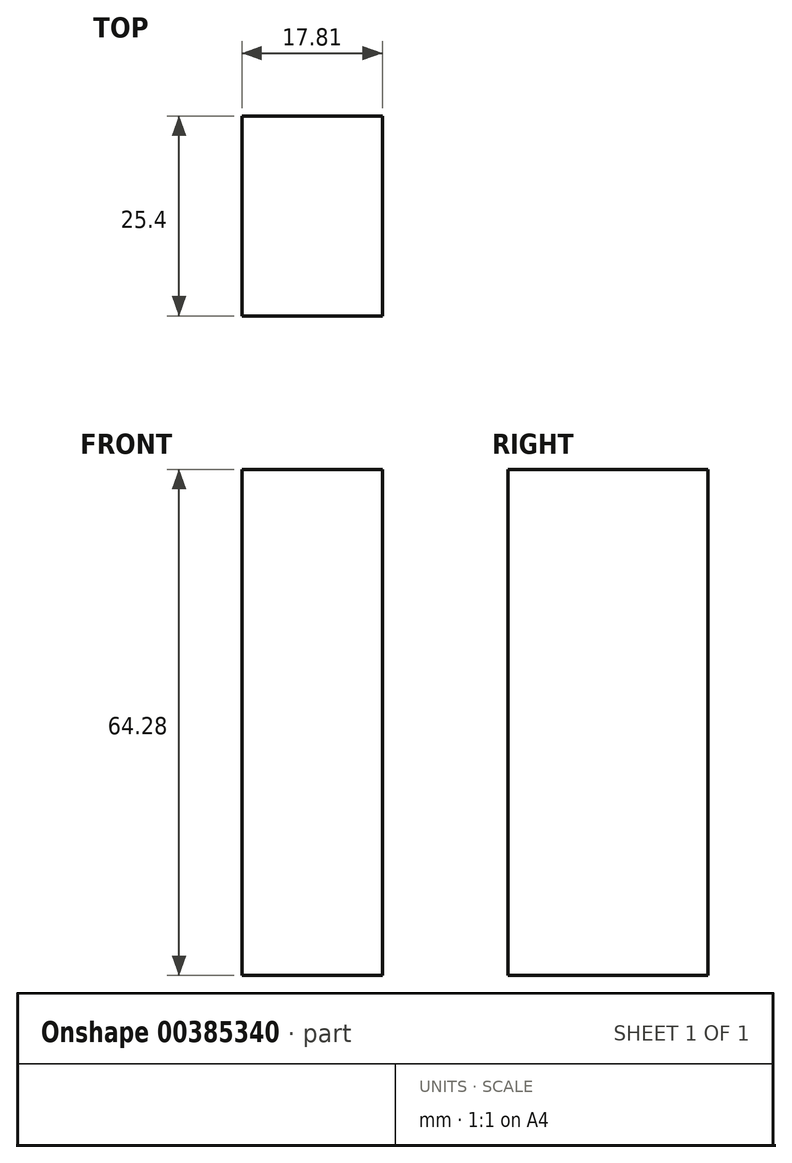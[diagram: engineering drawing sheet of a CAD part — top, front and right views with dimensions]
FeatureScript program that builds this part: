
annotation { "Feature Type Name" : "Feature", "Feature Type Description" : "" }
export const myFeature = defineFeature(function(context is Context, id is Id, definition is map)
    precondition{}
    {
        {
            var Q0;
            Q0=qCreatedBy(makeId("Front.planeOp"),FACE);
            var sketch = newSketch(context, id + "F0", { "sketchPlane" : qUnion([Q0])});
            skLineSegment(sketch, "E0.bottom", {"start": v(-9.79, -11.84) * mm, "end": v(8.02, -11.84) * mm});
            skLineSegment(sketch, "E0.top", {"start": v(-9.79, -76.12) * mm, "end": v(8.02, -76.12) * mm});
            skLineSegment(sketch, "E0.left", {"start": v(-9.79, -11.84) * mm, "end": v(-9.79, -76.12) * mm});
            skLineSegment(sketch, "E0.right", {"start": v(8.02, -11.84) * mm, "end": v(8.02, -76.12) * mm});
            skSolve(sketch);
        }
        {
            var Q0;
            Q0 = qSketchRegion(id + "F0", true);
            extrude(context, id + "F1", {"entities" : qUnion([Q0]), "endBound" : BoundingType.SYMMETRIC, "depth" : 25.4 * mm});
        }
    });
